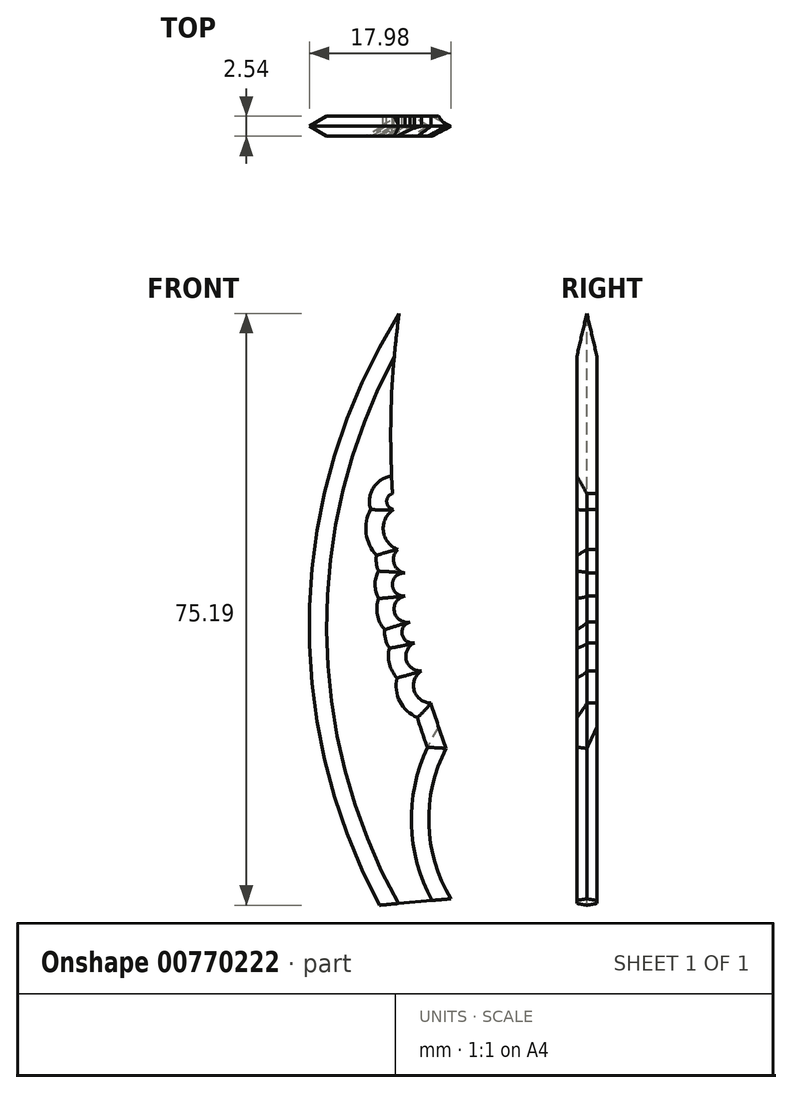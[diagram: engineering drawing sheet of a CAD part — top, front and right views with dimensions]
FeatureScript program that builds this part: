
annotation { "Feature Type Name" : "Feature", "Feature Type Description" : "" }
export const myFeature = defineFeature(function(context is Context, id is Id, definition is map)
    precondition{}
    {
        {
            var Q0;
            Q0=qCreatedBy(makeId("Front.planeOp"),FACE);
            var sketch = newSketch(context, id + "F0", { "sketchPlane" : qUnion([Q0])});
            skArc(sketch, "E0", {"start": v(-23.69, 42.68) * mm, "mid": v(-35.5, 5.07) * mm, "end": v(-26.68, -33.36) * mm});
            skArc(sketch, "E1", {"start": v(-23.69, 42.68) * mm, "mid": v(-24.79, 30.85) * mm, "end": v(-24.66, 18.97) * mm});
            skArc(sketch, "E2", {"start": v(-17.68, -13.84) * mm, "mid": v(-19.7, -23.26) * mm, "end": v(-16.86, -32.47) * mm});
            skArc(sketch, "E3", {"start": v(-23.1, 5.96) * mm, "mid": v(-24.43, 3.98) * mm, "end": v(-22.45, 2.64) * mm});
            skArc(sketch, "E4", {"start": v(-22.45, 2.64) * mm, "mid": v(-23.42, 1.04) * mm, "end": v(-21.86, 0) * mm});
            skArc(sketch, "E5", {"start": v(-21.86, 0) * mm, "mid": v(-22.92, -2.15) * mm, "end": v(-20.97, -3.55) * mm});
            skArc(sketch, "E6", {"start": v(-20.97, -3.55) * mm, "mid": v(-21.91, -6.04) * mm, "end": v(-19.79, -7.65) * mm});
            skArc(sketch, "E7", {"start": v(-24.52, 16.96) * mm, "mid": v(-25.83, 14.25) * mm, "end": v(-24, 11.86) * mm});
            skArc(sketch, "E8.trimOffspring", {"start": v(-19.79, -7.65) * mm, "mid": v(-18.78, -10.76) * mm, "end": v(-17.68, -13.84) * mm});
            skArc(sketch, "E9", {"start": v(-23.1, 8.86) * mm, "mid": v(-24.67, 7.4) * mm, "end": v(-23.1, 5.96) * mm});
            skArc(sketch, "E10", {"start": v(-24, 11.86) * mm, "mid": v(-24.46, 10.09) * mm, "end": v(-23.1, 8.86) * mm});
            skArc(sketch, "E11", {"start": v(-24.66, 18.97) * mm, "mid": v(-25.4, 17.9) * mm, "end": v(-24.52, 16.96) * mm});
            skLineSegment(sketch, "E12", {"start": v(-26.68, -33.36) * mm, "end": v(-16.86, -32.47) * mm});
            skSolve(sketch);
        }
        {
            var Q0;
            Q0 = qSketchRegion(id + "F0", true);
            extrude(context, id + "F1", {"entities" : qUnion([Q0]), "endBound" : BoundingType.SYMMETRIC, "depth" : 2.54 * mm, "offsetDistance" : 25.4 * mm});
        }
        {
            var Q0;
            Q0=makeQuery(id+"F1.opExtrude","CAP_EDGE",EDGE,{"disambiguationData":[OSD([sQuery(id+"F0.wireOp",EDGE,"E0")])],"isStart":false});
            var Q1;
            Q1=makeQuery(id+"F1.opExtrude","CAP_EDGE",EDGE,{"disambiguationData":[OSD([sQuery(id+"F0.wireOp",EDGE,"E2")])],"isStart":false});
            var Q2;
            Q2=makeQuery(id+"F1.opExtrude","CAP_EDGE",EDGE,{"disambiguationData":[OSD([sQuery(id+"F0.wireOp",EDGE,"E2")])],"isStart":true});
            var Q3;
            Q3=makeQuery(id+"F1.opExtrude","CAP_EDGE",EDGE,{"disambiguationData":[OSD([sQuery(id+"F0.wireOp",EDGE,"E0")])],"isStart":true});
            chamfer(context, id + "F2", {"entities" : qUnion([Q0, Q1, Q2, Q3]), "chamferType" : ChamferType.OFFSET_ANGLE, "width" : 2.54 * mm, "oppositeDirection" : false, "angle" : 30 * degree, "tangentPropagation" : true});
        }
        {
            var Q0;
            Q0=makeQuery(id+"F1.opExtrude","CAP_EDGE",EDGE,{"disambiguationData":[OSD([sQuery(id+"F0.wireOp",EDGE,"E11")])],"isStart":false});
            var Q1;
            Q1=makeQuery(id+"F1.opExtrude","CAP_EDGE",EDGE,{"disambiguationData":[OSD([sQuery(id+"F0.wireOp",EDGE,"E7")])],"isStart":false});
            var Q2;
            Q2=makeQuery(id+"F1.opExtrude","CAP_EDGE",EDGE,{"disambiguationData":[OSD([sQuery(id+"F0.wireOp",EDGE,"E10")])],"isStart":false});
            var Q3;
            Q3=makeQuery(id+"F1.opExtrude","CAP_EDGE",EDGE,{"disambiguationData":[OSD([sQuery(id+"F0.wireOp",EDGE,"E9")])],"isStart":false});
            var Q4;
            Q4=makeQuery(id+"F1.opExtrude","CAP_EDGE",EDGE,{"disambiguationData":[OSD([sQuery(id+"F0.wireOp",EDGE,"E3")])],"isStart":false});
            var Q5;
            Q5=makeQuery(id+"F1.opExtrude","CAP_EDGE",EDGE,{"disambiguationData":[OSD([sQuery(id+"F0.wireOp",EDGE,"E4")])],"isStart":false});
            var Q6;
            Q6=makeQuery(id+"F1.opExtrude","CAP_EDGE",EDGE,{"disambiguationData":[OSD([sQuery(id+"F0.wireOp",EDGE,"E5")])],"isStart":false});
            var Q7;
            Q7=makeQuery(id+"F1.opExtrude","CAP_EDGE",EDGE,{"disambiguationData":[OSD([sQuery(id+"F0.wireOp",EDGE,"E6")])],"isStart":false});
            var Q8;
            Q8=makeQuery(id+"F1.opExtrude","CAP_EDGE",EDGE,{"disambiguationData":[OSD([sQuery(id+"F0.wireOp",EDGE,"E8.trimOffspring")])],"isStart":false});
            chamfer(context, id + "F3", {"entities" : qUnion([Q0, Q1, Q2, Q3, Q4, Q5, Q6, Q7, Q8]), "chamferType" : ChamferType.OFFSET_ANGLE, "width" : 1.27 * mm, "oppositeDirection" : false, "angle" : 60 * degree, "tangentPropagation" : true});
        }
    });
